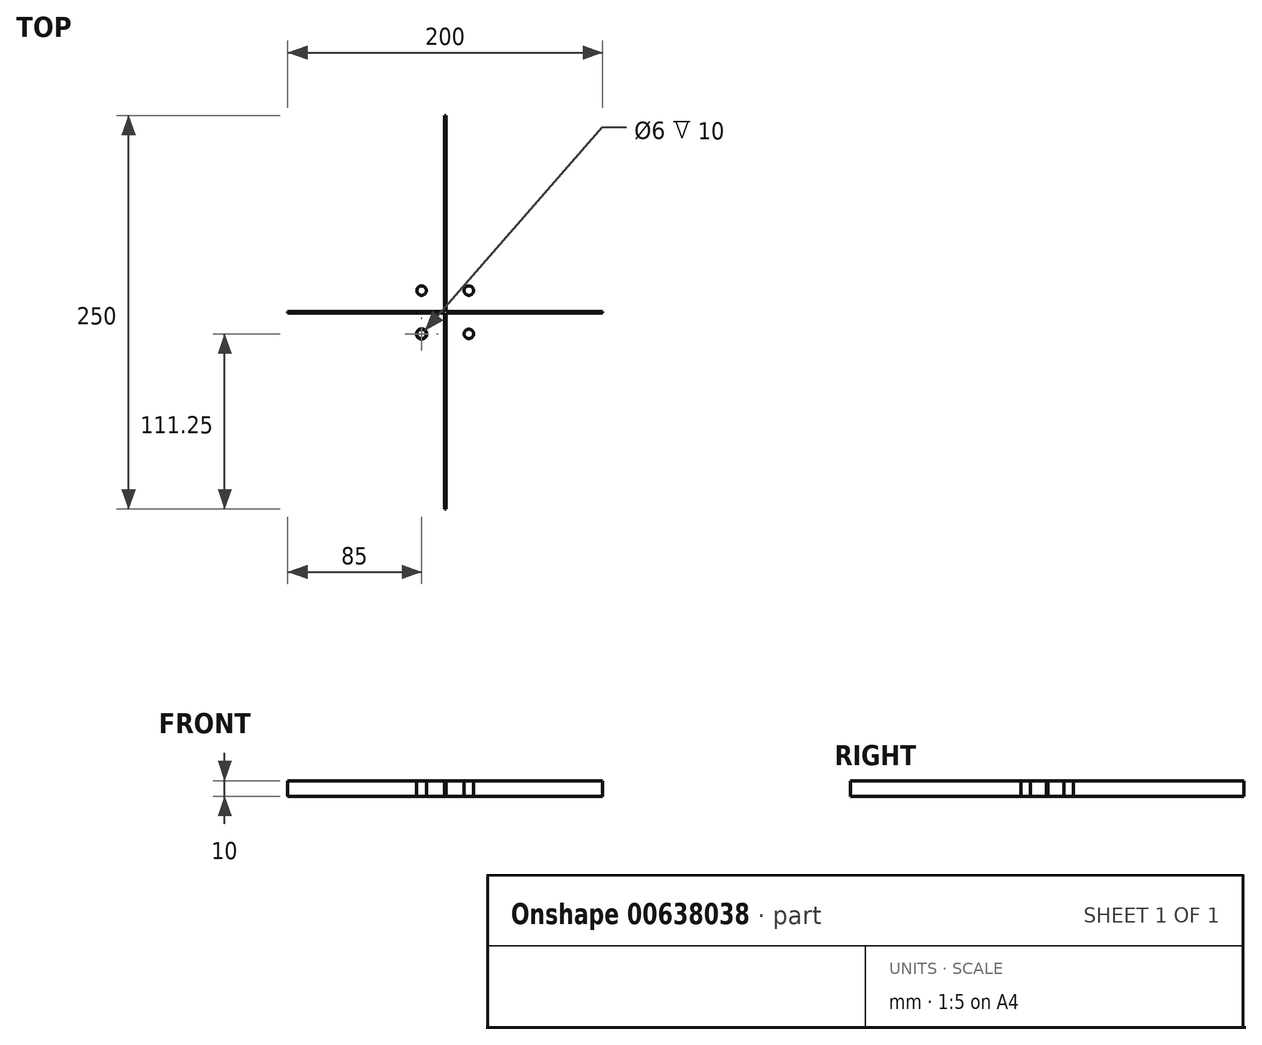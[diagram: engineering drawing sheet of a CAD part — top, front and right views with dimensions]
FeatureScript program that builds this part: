
annotation { "Feature Type Name" : "Feature", "Feature Type Description" : "" }
export const myFeature = defineFeature(function(context is Context, id is Id, definition is map)
    precondition{}
    {
        {
            var Q0;
            Q0=qCreatedBy(makeId("Top.planeOp"),FACE);
            var sketch = newSketch(context, id + "F0", { "sketchPlane" : qUnion([Q0])});
            skCircle(sketch, "E0", {"center": v(-15, 13.75) * mm, "radius": 3 * mm});
            skCircle(sketch, "E1.MirrorC", {"center": v(-15, -13.75) * mm, "radius": 3.25 * mm});
            skCircle(sketch, "E2.MirrorC", {"center": v(-15, -13.75) * mm, "radius": 3 * mm});
            skCircle(sketch, "E3.MirrorC", {"center": v(15, 13.75) * mm, "radius": 3 * mm});
            skCircle(sketch, "E4.MirrorC", {"center": v(15, -13.75) * mm, "radius": 3 * mm});
            skLineSegment(sketch, "E5", {"start": v(0, 0) * mm, "end": v(0, 100) * mm});
            skLineSegment(sketch, "E6.MirrorCS", {"start": v(0, -100) * mm, "end": v(0, 0) * mm});
            skLineSegment(sketch, "E7", {"start": v(0, 0) * mm, "end": v(-100, 0) * mm});
            skLineSegment(sketch, "E8.MirrorCS", {"start": v(0, 0) * mm, "end": v(100, 0) * mm});
            skLineSegment(sketch, "E9.bottom", {"start": v(-0.5, 125) * mm, "end": v(0.5, 125) * mm});
            skLineSegment(sketch, "E9.top", {"start": v(-0.5, -125) * mm, "end": v(0.5, -125) * mm});
            skLineSegment(sketch, "E9.left", {"start": v(-0.5, 125) * mm, "end": v(-0.5, -125) * mm});
            skLineSegment(sketch, "E9.right", {"start": v(0.5, 125) * mm, "end": v(0.5, -125) * mm});
            skPoint(sketch, "E9.middle", {"position": v(0, 0) * mm});
            skLineSegment(sketch, "E10.bottom", {"start": v(-100, 0.5) * mm, "end": v(100, 0.5) * mm});
            skLineSegment(sketch, "E10.top", {"start": v(-100, -0.5) * mm, "end": v(100, -0.5) * mm});
            skLineSegment(sketch, "E10.left", {"start": v(-100, 0.5) * mm, "end": v(-100, -0.5) * mm});
            skLineSegment(sketch, "E10.right", {"start": v(100, 0.5) * mm, "end": v(100, -0.5) * mm});
            skSolve(sketch);
        }
        {
            var Q0;
            Q0 = qSketchRegion(id + "F0", true);
            extrude(context, id + "F1", {"entities" : qUnion([Q0]), "depth" : 10 * mm, "offsetDistance" : 25 * mm});
        }
    });
